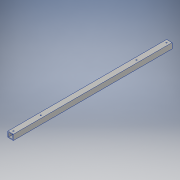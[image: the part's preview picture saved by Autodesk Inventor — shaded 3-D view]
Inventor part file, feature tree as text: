
AUTODESK INVENTOR PART (.ipt)
format: ipt  version: 2018 (Build 220112000, 112)  size: 134,144 bytes
history: native  units: in
note: dims shown in document units (in); Inventor stores cm internally (conversion verified against a paired STEP export)
features: extrude x4, sketch x4
ambient origin geometry x8: Origin, YZ Plane, XZ Plane, XY Plane, X Axis, Y Axis, Z Axis, Center Point
bodies: Solid1 (feature_tree)
feature tree (8):
  extrude  "Extrusion1"  Depth=29.0in
  extrude  "Extrusion2"  Depth=0.125in
  extrude  "Extrusion3"  Depth=0.75in
  extrude  "Extrusion4"  Depth=6.5in TaperAngle=0.0deg
  sketch  "Sketch1"  dims[d0=1.0in d1=29.0in]
  sketch  "Sketch2"  dims[d2=1.0in d3=0.0in d4=0.125in]
  sketch  "Sketch3"  dims[d5=0.125in d6=0.75in]
  sketch  "Sketch4"  dims[d7=0.75in d8=6.5in d9=0.0in d10=6.0in d11=0.5in d12=0.5in d13=0.2in d14=1.0in d15=0.0in d16=0.5in d17=0.5in d18=6.0in d19=0.5in d20=0.2in d21=1.0in d22=0.0in]
